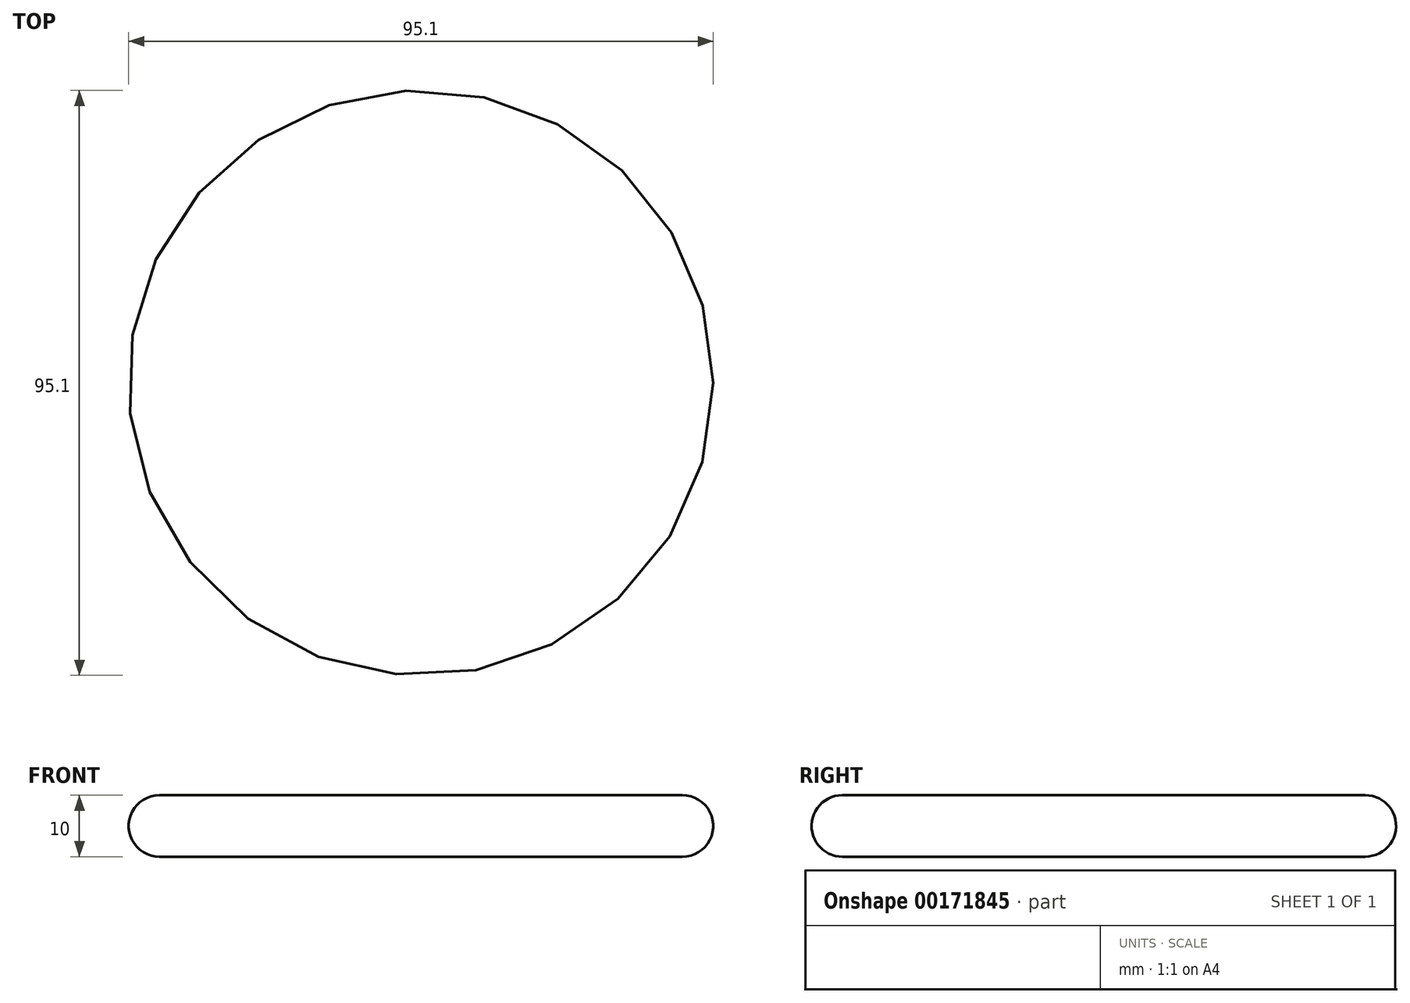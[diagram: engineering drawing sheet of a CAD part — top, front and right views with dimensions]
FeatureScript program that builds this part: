
annotation { "Feature Type Name" : "Feature", "Feature Type Description" : "" }
export const myFeature = defineFeature(function(context is Context, id is Id, definition is map)
    precondition{}
    {
        {
            var Q0;
            Q0=qCreatedBy(makeId("Top.planeOp"),FACE);
            var sketch = newSketch(context, id + "F0", { "sketchPlane" : qUnion([Q0])});
            skCircle(sketch, "E0", {"center": v(0, 0) * mm, "radius": 47.55 * mm});
            skSolve(sketch);
        }
        {
            var Q0;
            Q0=qSketchRegion(id+"F0",true);
            extrude(context, id + "F1", {"entities" : qUnion([Q0]), "depth" : 10 * mm});
        }
        {
            var Q0;
            Q0=makeQuery(id+"F1.opExtrude","CAP_EDGE",EDGE,{"disambiguationData":[OSD([sQuery(id+"F0.wireOp",EDGE,"E0")])],"isStart":false});
            fillet(context, id + "F2", {"entities" : qUnion([Q0]), "radius" : 5 * mm, "tangentPropagation" : true, "allowEdgeOverflow" : false});
        }
        {
            var Q0;
            Q0=makeQuery(id+"F1.opExtrude","CAP_EDGE",EDGE,{"disambiguationData":[OSD([sQuery(id+"F0.wireOp",EDGE,"E0")])],"isStart":true});
            fillet(context, id + "F3", {"entities" : qUnion([Q0]), "radius" : 5 * mm, "tangentPropagation" : true, "allowEdgeOverflow" : false});
        }
    });
